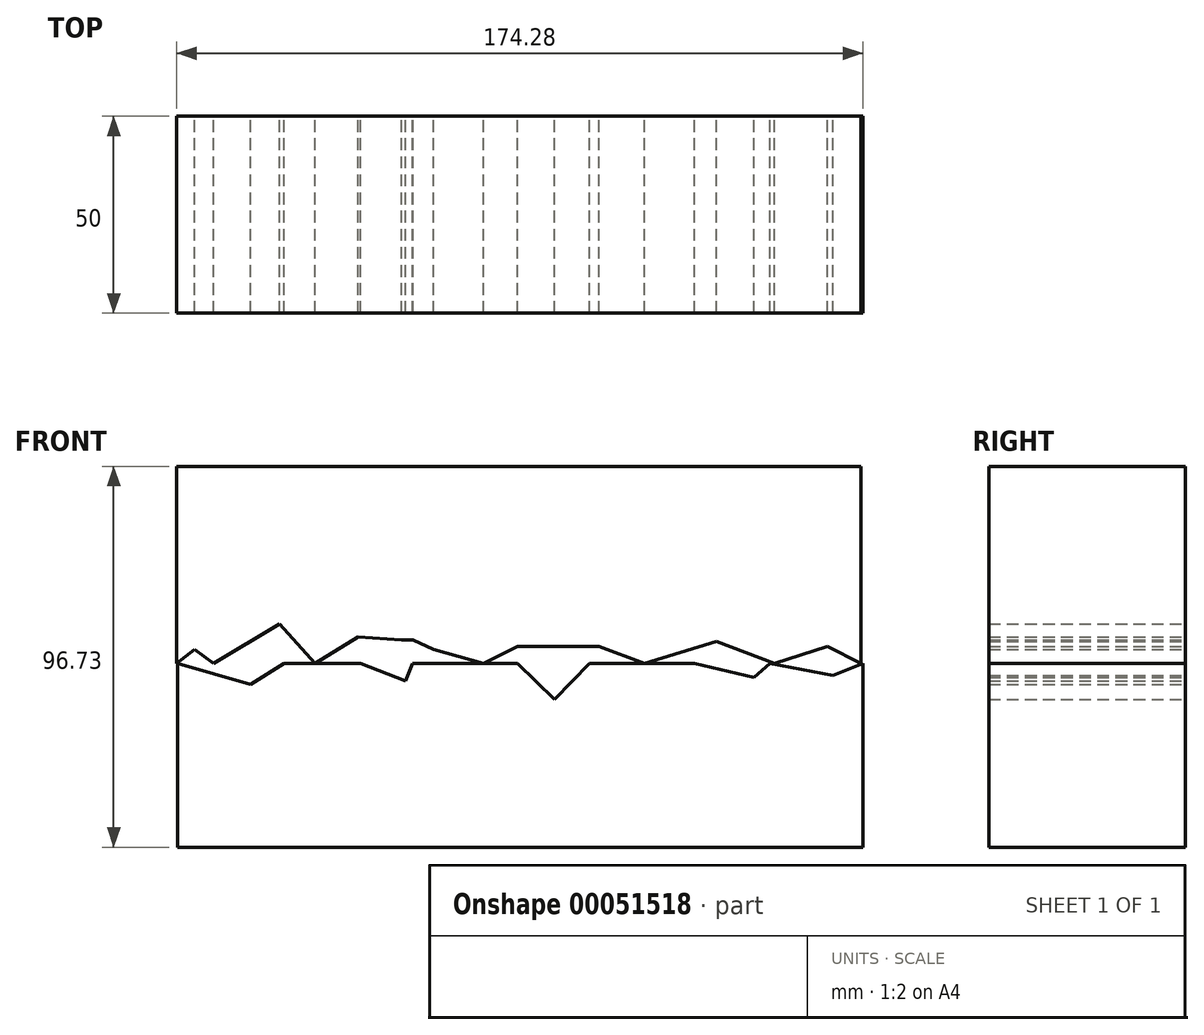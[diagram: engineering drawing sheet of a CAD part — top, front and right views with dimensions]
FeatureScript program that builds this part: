
annotation { "Feature Type Name" : "Feature", "Feature Type Description" : "" }
export const myFeature = defineFeature(function(context is Context, id is Id, definition is map)
    precondition{}
    {
        {
            var Q0;
            Q0=qCreatedBy(makeId("Front.planeOp"),FACE);
            var sketch = newSketch(context, id + "F0", { "sketchPlane" : qUnion([Q0])});
            skLineSegment(sketch, "E0", {"start": v(-77.14, 0) * mm, "end": v(-60.4, 10) * mm});
            skLineSegment(sketch, "E1", {"start": v(-60.4, 10) * mm, "end": v(-51.43, 0) * mm});
            skLineSegment(sketch, "E2", {"start": v(-51.43, 0) * mm, "end": v(-40.4, 6.73) * mm});
            skLineSegment(sketch, "E3", {"start": v(-40.4, 6.73) * mm, "end": v(-29.39, 5.92) * mm});
            skLineSegment(sketch, "E4", {"start": v(-29.39, 5.92) * mm, "end": v(-26.53, 5.92) * mm});
            skLineSegment(sketch, "E5", {"start": v(-26.53, 5.92) * mm, "end": v(-21.22, 3.47) * mm});
            skLineSegment(sketch, "E6", {"start": v(-21.22, 3.47) * mm, "end": v(-8.57, 0) * mm});
            skLineSegment(sketch, "E7", {"start": v(-8.57, 0) * mm, "end": v(0, 4.29) * mm});
            skLineSegment(sketch, "E8", {"start": v(0, 4.29) * mm, "end": v(20.82, 4.29) * mm});
            skLineSegment(sketch, "E9", {"start": v(20.82, 4.29) * mm, "end": v(32.24, 0) * mm});
            skLineSegment(sketch, "E10", {"start": v(32.24, 0) * mm, "end": v(50.61, 5.51) * mm});
            skLineSegment(sketch, "E11", {"start": v(50.61, 5.51) * mm, "end": v(65.3, 0) * mm});
            skLineSegment(sketch, "E12", {"start": v(65.3, 0) * mm, "end": v(78.78, 4.29) * mm});
            skLineSegment(sketch, "E13", {"start": v(78.78, 4.29) * mm, "end": v(87.35, 0) * mm});
            skLineSegment(sketch, "E14", {"start": v(87.35, 0) * mm, "end": v(87.35, 50) * mm});
            skLineSegment(sketch, "E15", {"start": v(87.35, 50) * mm, "end": v(-86.53, 50) * mm});
            skLineSegment(sketch, "E16", {"start": v(-86.53, 50) * mm, "end": v(-86.53, 0) * mm});
            skLineSegment(sketch, "E17", {"start": v(-86.53, 0) * mm, "end": v(-82.04, 3.47) * mm});
            skLineSegment(sketch, "E18", {"start": v(-82.04, 3.47) * mm, "end": v(-77.14, 0) * mm});
            skSolve(sketch);
        }
        {
            var Q0;
            Q0=qCreatedBy(makeId("Front.planeOp"),FACE);
            var sketch = newSketch(context, id + "F1", { "sketchPlane" : qUnion([Q0])});
            skLineSegment(sketch, "E19", {"start": v(-86.35, 0) * mm, "end": v(-67.72, -5.39) * mm});
            skLineSegment(sketch, "E20", {"start": v(-67.72, -5.39) * mm, "end": v(-59.27, 0) * mm});
            skLineSegment(sketch, "E21", {"start": v(-59.27, 0) * mm, "end": v(-39.77, 0) * mm});
            skLineSegment(sketch, "E22", {"start": v(-39.77, 0) * mm, "end": v(-28.41, -4.51) * mm});
            skLineSegment(sketch, "E23", {"start": v(-28.41, -4.51) * mm, "end": v(-26.62, 0) * mm});
            skLineSegment(sketch, "E24", {"start": v(-26.62, 0) * mm, "end": v(0, 0) * mm});
            skLineSegment(sketch, "E25", {"start": v(0, 0) * mm, "end": v(9.43, -9.17) * mm});
            skLineSegment(sketch, "E26", {"start": v(9.43, -9.17) * mm, "end": v(18.35, 0) * mm});
            skLineSegment(sketch, "E27", {"start": v(18.35, 0) * mm, "end": v(44.95, 0) * mm});
            skLineSegment(sketch, "E28", {"start": v(44.95, 0) * mm, "end": v(60.09, -3.64) * mm});
            skLineSegment(sketch, "E29", {"start": v(60.09, -3.64) * mm, "end": v(64.17, 0) * mm});
            skLineSegment(sketch, "E30", {"start": v(64.17, 0) * mm, "end": v(80.18, -3.06) * mm});
            skLineSegment(sketch, "E31", {"start": v(80.18, -3.06) * mm, "end": v(87.75, 0) * mm});
            skLineSegment(sketch, "E32", {"start": v(87.75, 0) * mm, "end": v(87.75, -46.73) * mm});
            skLineSegment(sketch, "E33", {"start": v(87.75, -46.73) * mm, "end": v(-86.35, -46.73) * mm});
            skLineSegment(sketch, "E34", {"start": v(-86.35, -46.73) * mm, "end": v(-86.35, 0) * mm});
            skSolve(sketch);
        }
        {
            var Q0;
            Q0=makeQuery(id+"F0.imprint","IMPRINT",FACE,{"disambiguationData":[TD([[makeQuery(id+"F0.imprint","IMPRINT",EDGE,{"derivedFrom":sQuery(id+"F0.wireOp",EDGE,"E0")}),1.0]])]});
            extrude(context, id + "F2", {"entities" : qUnion([Q0]), "depth" : 50 * mm});
        }
        {
            var Q0;
            Q0=makeQuery(id+"F1.imprint","IMPRINT",FACE,{"disambiguationData":[TD([[makeQuery(id+"F1.imprint","IMPRINT",EDGE,{"derivedFrom":sQuery(id+"F1.wireOp",EDGE,"E19")}),-1.0]])]});
            extrude(context, id + "F3", {"entities" : qUnion([Q0]), "depth" : 50 * mm});
        }
    });
